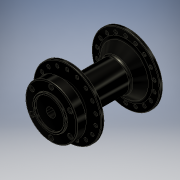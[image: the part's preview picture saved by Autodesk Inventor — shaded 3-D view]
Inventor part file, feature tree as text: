
AUTODESK INVENTOR PART (.ipt)
format: ipt  version: 2017 (Build 210142000, 142)  size: 485,888 bytes
history: native  units: mm
features: chamfer x6, fillet x5, sketch x5, extrude x4, pattern_circular x2, revolve x1, hole x1
ambient origin geometry x8: Origin, YZ Plane, XZ Plane, XY Plane, X Axis, Y Axis, Z Axis, Center Point
bodies: Body1 (feature_tree)
feature tree (24):
  revolve  "Revolution1"  [1 undecoded]
  chamfer  "Chamfer1"  Distance=3.42mm
  fillet  "Fillet1"  Radius=6.0mm
  extrude  "Extrusion2"  Depth=2.0mm
  chamfer  "Chamfer2"  Distance=19.58mm
  pattern_circular  "Circular Pattern1"  [2 undecoded]
  extrude  "Extrusion3"  TaperAngle=90.0deg  [1 undecoded]
  chamfer  "Chamfer3"  Distance=10.0mm Angle=45.0deg
  pattern_circular  "Circular Pattern2"  [2 undecoded]
  extrude  "Extrusion4"  Depth=2.0mm
  chamfer  "Chamfer4"  Distance=5.0mm
  fillet  "Fillet2"  [1 undecoded]
  fillet  "Fillet3"  Radius=2.0mm
  fillet  "Fillet4"  Radius=180.0mm
  fillet  "Fillet5"  Radius=4.01mm
  extrude  "Extrusion5"  Depth=2.0mm
  hole  "Hole1"  [1 undecoded]
  chamfer  "Chamfer5"  Distance=2.0mm Angle=45.0deg
  chamfer  "Chamfer6"  Distance=60.0mm Angle=360.0deg
  sketch  "Sketch1"  dims[d3=15.0mm d4=55.0mm]
  sketch  "Sketch4"  dims[d5=34.0mm]
  sketch  "Sketch5"  dims[d6=34.0mm]
  sketch  "Sketch6"  dims[d7=21.5mm]
  sketch  "Sketch7"  dims[d8=3.42mm d9=3.42mm d10=6.0mm d11=26.0mm d12=19.58mm d13=17.5mm d14=90.0deg d15=10.0mm d16=2.0mm d17=45.0deg d18=4.0mm d19=2.7mm d21=5.0mm d22=0.0mm d23=0.0mm d24=0.5mm d25=2.0mm d26=45.0deg d27=180.0mm d28=360.0deg d30=4.01mm d31=4.0mm d32=10.0mm d33=0.0mm d34=0.5mm d35=2.0mm d36=45.0deg d37=60.0mm d38=360.0deg d40=38.0mm d41=29.0mm d42=2.0mm d43=0.0mm d44=5.0mm d45=2.0mm d46=3.804818mm d47=6.0mm d48=2.0mm d49=1.0mm d50=0.6mm d51=32.8mm d52=29.0mm d53=2.0mm d54=0.0mm d55=10.0mm d56=10.0mm d57=9.02mm d58=6.0mm d59=4.0mm d60=2.0mm d61=90.0deg d62=8.0mm d63=20.594885mm d64=0.3mm d65=2.0mm d66=45.0deg d67=0.3mm d68=2.0mm d69=45.0deg]
note: 8 required parameter values undecoded (feature->parameter linkage not recoverable at this tier; creation-order binding heuristic only, values carry confidence <= 0.55)